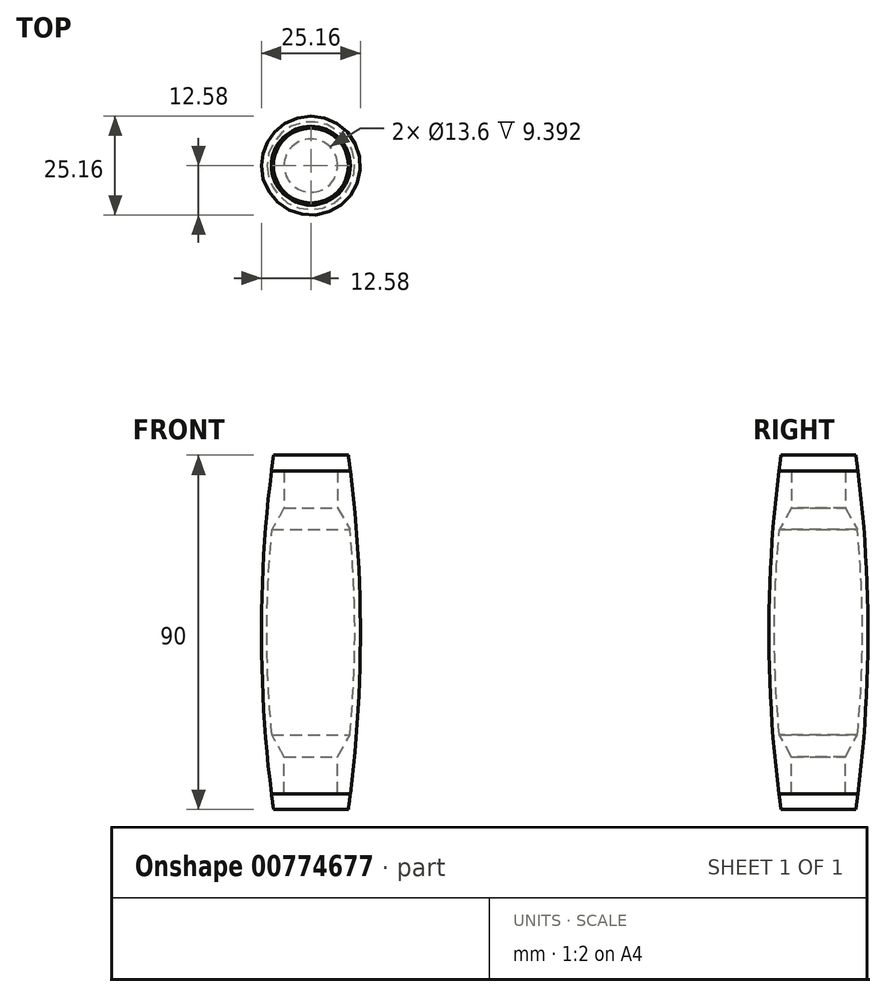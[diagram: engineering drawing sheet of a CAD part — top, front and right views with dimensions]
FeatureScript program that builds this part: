
annotation { "Feature Type Name" : "Feature", "Feature Type Description" : "" }
export const myFeature = defineFeature(function(context is Context, id is Id, definition is map)
    precondition{}
    {
        {
            var Q0;
            Q0=qCreatedBy(makeId("Front.planeOp"),FACE);
            var sketch = newSketch(context, id + "F0", { "sketchPlane" : qUnion([Q0])});
            skPoint(sketch, "E0.middle", {"position": v(0, 0) * mm});
            skLineSegment(sketch, "E1.bottom", {"start": v(0, -45) * mm, "end": v(-9.5, -45) * mm});
            skLineSegment(sketch, "E1.top", {"start": v(0, 45) * mm, "end": v(-12.5, 45) * mm});
            skPoint(sketch, "E2", {"position": v(-9.5, 45) * mm});
            skPoint(sketch, "E3.MirrorP", {"position": v(-9.5, -45) * mm});
            skPoint(sketch, "E4", {"position": v(-12.5, 0) * mm});
            skArc(sketch, "E5", {"start": v(-9.5, 45) * mm, "mid": v(-12.58, 2) * mm, "end": v(-10.02, -41.04) * mm});
            skPoint(sketch, "E6", {"position": v(0, 45) * mm});
            skPoint(sketch, "E7", {"position": v(0, -45) * mm});
            skPoint(sketch, "E8.orphan", {"position": v(12.5, 45) * mm});
            skLineSegment(sketch, "E9", {"start": v(-6.8, 31.65) * mm, "end": v(-9.9, 26.11) * mm});
            skArc(sketch, "E10.trimOffspring", {"start": v(-9.9, 26.11) * mm, "mid": v(-11.16, 0) * mm, "end": v(-9.9, -26.11) * mm});
            skPoint(sketch, "E11.orphan", {"position": v(0, -41) * mm});
            skLineSegment(sketch, "E12.MirrorCS", {"start": v(-6.8, -31.65) * mm, "end": v(-9.9, -26.11) * mm});
            skPoint(sketch, "E13.end.orphan", {"position": v(-10.02, 41.04) * mm});
            skLineSegment(sketch, "E14", {"start": v(-6.8, 31.65) * mm, "end": v(-6.8, 41.04) * mm});
            skLineSegment(sketch, "E15", {"start": v(-6.8, 41.04) * mm, "end": v(-10.02, 41.04) * mm});
            skLineSegment(sketch, "E16", {"start": v(-6.8, 31.65) * mm, "end": v(0, 31.65) * mm});
            skLineSegment(sketch, "E17", {"start": v(0, 31.65) * mm, "end": v(0, 45) * mm});
            skPoint(sketch, "E18.MirrorCS.end.orphan", {"position": v(-10.02, -41.04) * mm});
            skLineSegment(sketch, "E19.MirrorCS", {"start": v(-6.8, -31.65) * mm, "end": v(-6.8, -41.04) * mm});
            skLineSegment(sketch, "E20.MirrorCS", {"start": v(-6.8, -41.04) * mm, "end": v(-10.02, -41.04) * mm});
            skSolve(sketch);
        }
        {
            var Q0;
            Q0=makeQuery(id+"F0.imprint","IMPRINT",FACE,{"disambiguationData":[TD([[makeQuery(id+"F0.imprint","IMPRINT",EDGE,{"derivedFrom":sQuery(id+"F0.wireOp",EDGE,"E9")}),-1.0]])]});
            var Q1;
            Q1=sQuery(id+"F0.wireOp",EDGE,"E17");
            revolve(context, id + "F1", {"surfaceOperationType" : NewSurfaceOperationType.NEW, "entities" : qUnion([Q0]), "axis" : qUnion([Q1]), "revolveType" : RevolveType.FULL});
        }
        {
            var Q0;
            Q0=makeQuery(id+"F0.imprint","IMPRINT",FACE,{"disambiguationData":[TD([[makeQuery(id+"F0.imprint","IMPRINT",EDGE,{"derivedFrom":sQuery(id+"F0.wireOp",EDGE,"E14")}),-1.0]])]});
            var Q1;
            Q1=sQuery(id+"F0.wireOp",EDGE,"E17");
            revolve(context, id + "F2", {"surfaceOperationType" : NewSurfaceOperationType.NEW, "entities" : qUnion([Q0]), "axis" : qUnion([Q1]), "revolveType" : RevolveType.FULL});
        }
        {
            var Q0;
            Q0=makeQuery(id+"F2.opRevolve","SWEPT_BODY",BODY,{"disambiguationData":[OSD([sQuery(id+"F0.wireOp",EDGE,"E1.top"),sQuery(id+"F0.wireOp",EDGE,"E5"),sQuery(id+"F0.wireOp",EDGE,"EQru6bDl-febc-Y8y8-cLsO-kIyznJhBBkLX"),sQuery(id+"F0.wireOp",EDGE,"E13"),sQuery(id+"F0.wireOp",EDGE,"XuYF9uJ4-9Dts-T87d-6AJ1-bvazOsL9PkqU"),sQuery(id+"F0.wireOp",EDGE,"CTLsHvUB-fQmM-clcb-CuU5-zjeVhmAh7Ipj"),sQuery(id+"F0.wireOp",EDGE,"6iunlVhr-M3FV-LlYb-Eczb-EJaoZk5pZ2D2"),sQuery(id+"F0.wireOp",EDGE,"7141c618-31aa-47ae-a9c1-bedcf759e697.trimOffspring")])]});
            var Q1;
            Q1=qCreatedBy(makeId("Top.planeOp"),FACE);
            mirror(context, id + "F3", {"entities" : qUnion([Q0]), "mirrorPlane" : qUnion([Q1])});
        }
    });
